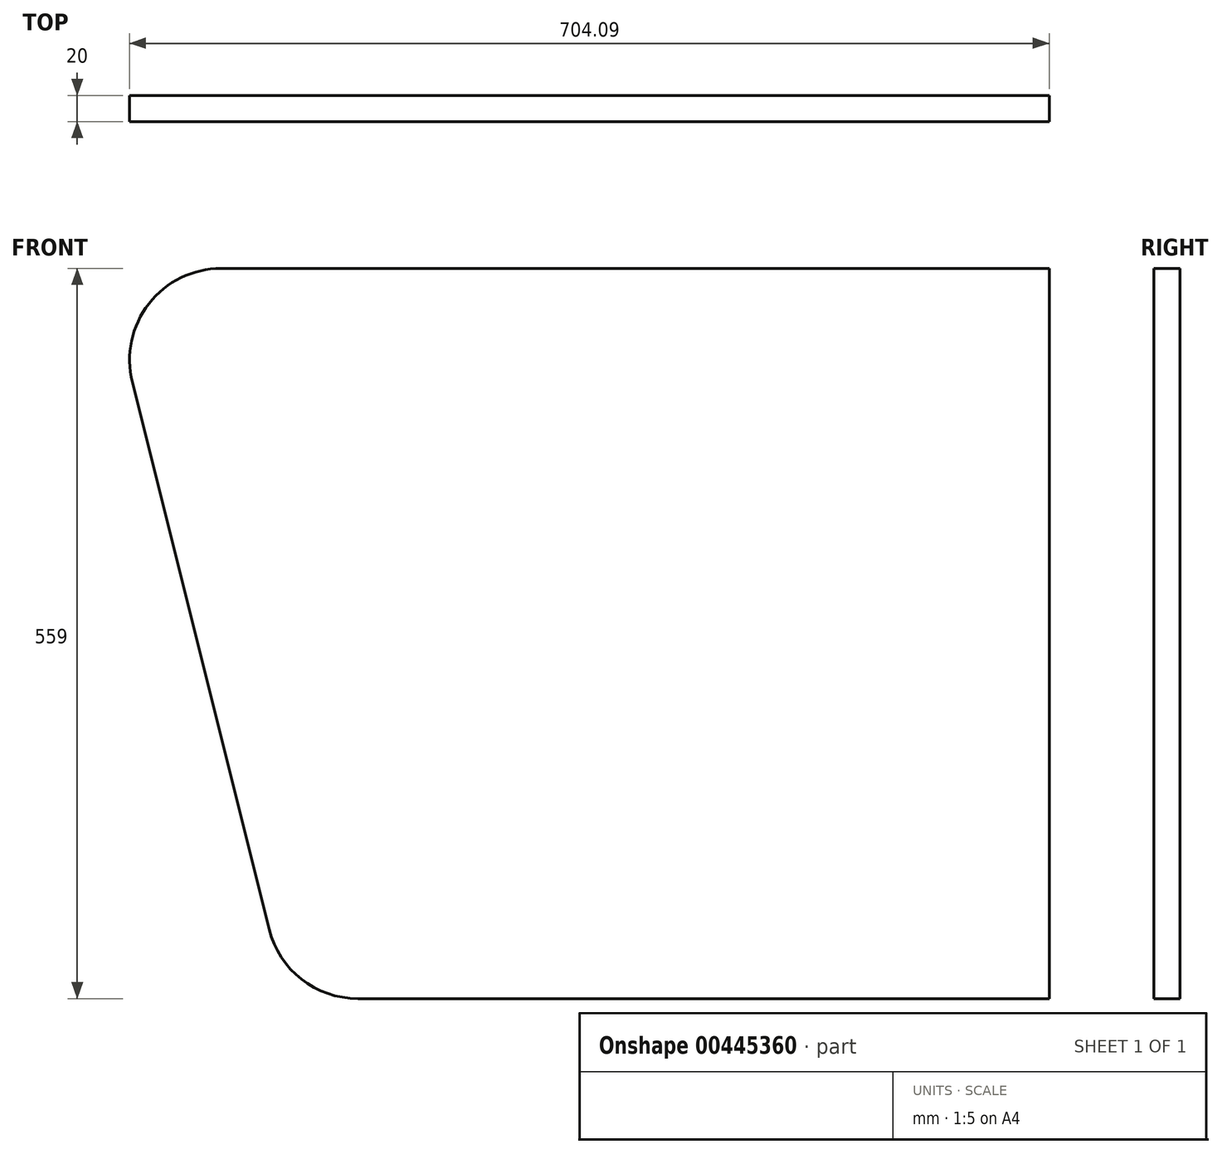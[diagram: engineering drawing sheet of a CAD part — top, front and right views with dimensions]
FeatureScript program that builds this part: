
annotation { "Feature Type Name" : "Feature", "Feature Type Description" : "" }
export const myFeature = defineFeature(function(context is Context, id is Id, definition is map)
    precondition{}
    {
        {
            var Q0;
            Q0=qCreatedBy(makeId("Front.planeOp"),FACE);
            var sketch = newSketch(context, id + "F0", { "sketchPlane" : qUnion([Q0])});
            skLineSegment(sketch, "E0.0", {"start": v(-634.09, 579.5) * mm, "end": v(0, 579.5) * mm});
            skLineSegment(sketch, "E0.1", {"start": v(-597.25, 73.52) * mm, "end": v(-702, 492.52) * mm});
            skLineSegment(sketch, "E0.2", {"start": v(0, 20.5) * mm, "end": v(-529.34, 20.5) * mm});
            skPoint(sketch, "E1.visualSharp", {"position": v(-723.74, 579.5) * mm});
            skArc(sketch, "E1.filletArc", {"start": v(-634.09, 579.5) * mm, "mid": v(-689.26, 552.58) * mm, "end": v(-702, 492.52) * mm});
            skPoint(sketch, "E2.visualSharp", {"position": v(-584, 20.5) * mm});
            skArc(sketch, "E2.filletArc", {"start": v(-597.25, 73.52) * mm, "mid": v(-572.42, 35.33) * mm, "end": v(-529.34, 20.5) * mm});
            skLineSegment(sketch, "E3", {"start": v(0, 579.5) * mm, "end": v(0, 20.5) * mm});
            skSolve(sketch);
        }
        {
            var Q0;
            Q0 = qSketchRegion(id + "F0", true);
            extrude(context, id + "F1", {"entities" : qUnion([Q0]), "depth" : 20 * mm});
        }
    });
